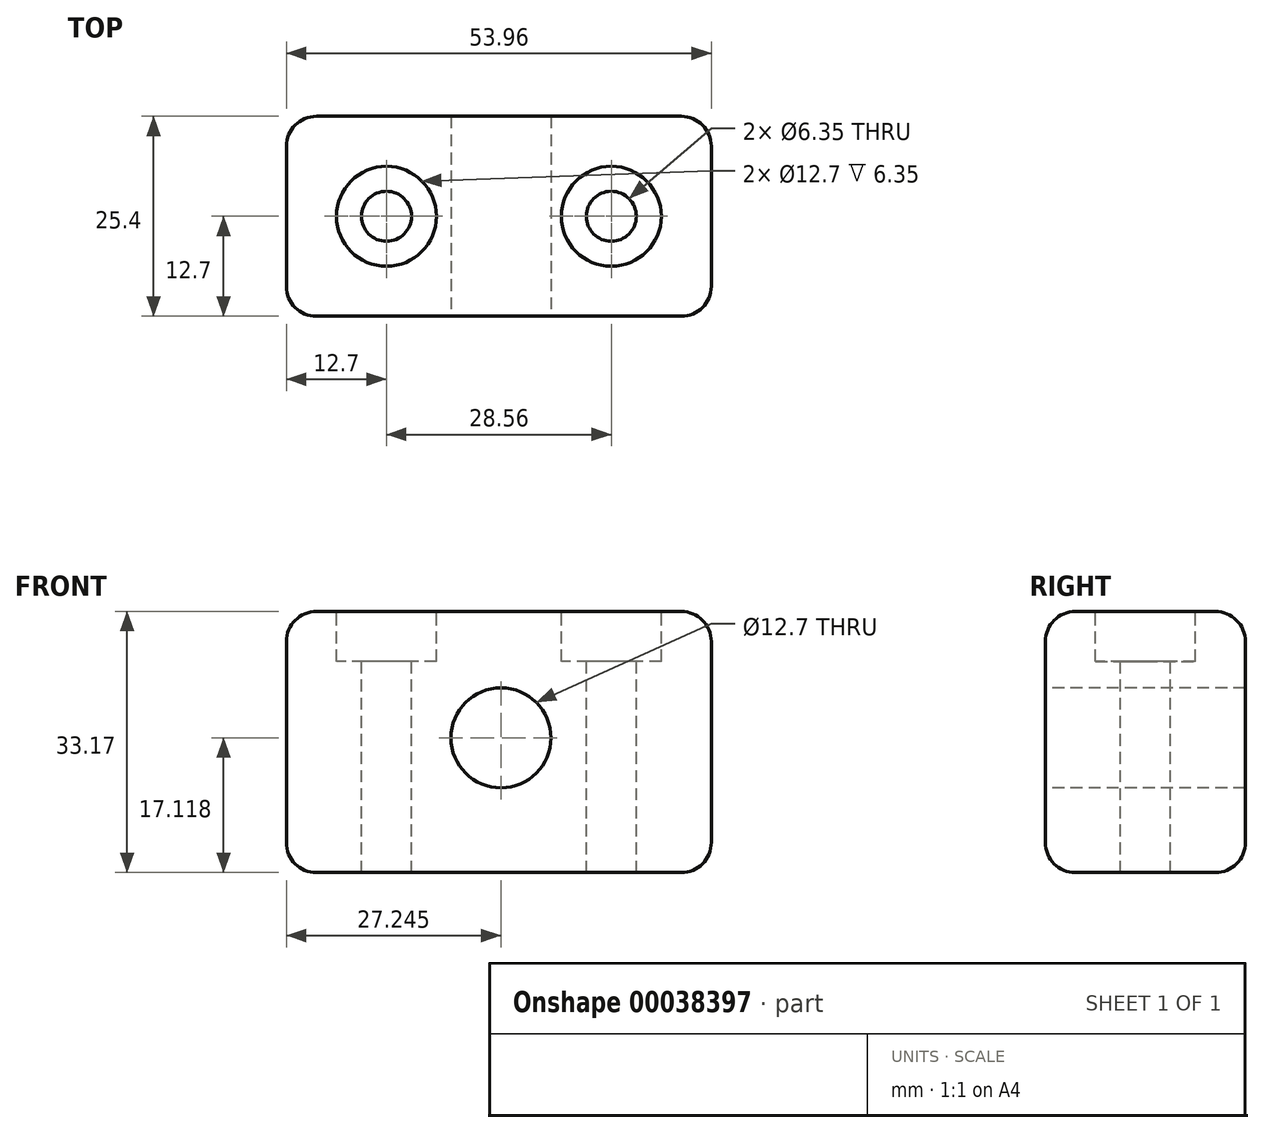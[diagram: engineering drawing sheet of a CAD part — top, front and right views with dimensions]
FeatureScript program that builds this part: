
annotation { "Feature Type Name" : "Feature", "Feature Type Description" : "" }
export const myFeature = defineFeature(function(context is Context, id is Id, definition is map)
    precondition{}
    {
        {
            var Q0;
            Q0=qCreatedBy(makeId("Front.planeOp"),FACE);
            var sketch = newSketch(context, id + "F0", { "sketchPlane" : qUnion([Q0])});
            skLineSegment(sketch, "E0.bottom", {"start": v(0, 0) * mm, "end": v(53.96, 0) * mm});
            skLineSegment(sketch, "E0.top", {"start": v(0, 33.17) * mm, "end": v(53.96, 33.17) * mm});
            skLineSegment(sketch, "E0.left", {"start": v(0, 0) * mm, "end": v(0, 33.17) * mm});
            skLineSegment(sketch, "E0.right", {"start": v(53.96, 0) * mm, "end": v(53.96, 33.17) * mm});
            skSolve(sketch);
        }
        {
            var Q0;
            Q0=makeQuery(id+"F0.imprint","IMPRINT",FACE,{"disambiguationData":[TD([[makeQuery(id+"F0.imprint","IMPRINT",EDGE,{"derivedFrom":sQuery(id+"F0.wireOp",EDGE,"E0.bottom")}),1.0]])]});
            extrude(context, id + "F1", {"entities" : qUnion([Q0]), "depth" : 25.4 * mm});
        }
        {
            var Q0;
            Q0=makeQuery(id+"F1.opExtrude","CAP_EDGE",EDGE,{"disambiguationData":[OSD([sQuery(id+"F0.wireOp",EDGE,"E0.top")])],"isStart":false});
            var Q1;
            Q1=makeQuery(id+"F1.opExtrude","SWEPT_EDGE",EDGE,{"disambiguationData":[OSD([sQuery(id+"F0.wireOp",EDGE,"E0.top"),sQuery(id+"F0.wireOp",EDGE,"E0.right")])]});
            var Q2;
            Q2=makeQuery(id+"F1.opExtrude","CAP_FACE",FACE,{"disambiguationData":[OSD([sQuery(id+"F0.wireOp",EDGE,"E0.bottom"),sQuery(id+"F0.wireOp",EDGE,"E0.top"),sQuery(id+"F0.wireOp",EDGE,"E0.left"),sQuery(id+"F0.wireOp",EDGE,"E0.right")])],"isStart":false});
            var Q3;
            Q3=makeQuery(id+"F1.opExtrude","SWEPT_FACE",FACE,{"disambiguationData":[OSD([sQuery(id+"F0.wireOp",EDGE,"E0.right")])]});
            var Q4;
            Q4=makeQuery(id+"F1.opExtrude","CAP_FACE",FACE,{"disambiguationData":[OSD([sQuery(id+"F0.wireOp",EDGE,"E0.bottom"),sQuery(id+"F0.wireOp",EDGE,"E0.top"),sQuery(id+"F0.wireOp",EDGE,"E0.left"),sQuery(id+"F0.wireOp",EDGE,"E0.right")])],"isStart":true});
            var Q5;
            Q5=makeQuery(id+"F1.opExtrude","SWEPT_FACE",FACE,{"disambiguationData":[OSD([sQuery(id+"F0.wireOp",EDGE,"E0.left")])]});
            fillet(context, id + "F2", {"entities" : qUnion([Q0, Q1, Q2, Q3, Q4, Q5]), "radius" : 3.8 * mm, "tangentPropagation" : true, "allowEdgeOverflow" : false});
        }
        {
            var Q0;
            Q0=makeQuery(id+"F1.opExtrude","CAP_FACE",FACE,{"disambiguationData":[OSD([sQuery(id+"F0.wireOp",EDGE,"E0.bottom"),sQuery(id+"F0.wireOp",EDGE,"E0.top"),sQuery(id+"F0.wireOp",EDGE,"E0.left"),sQuery(id+"F0.wireOp",EDGE,"E0.right")])],"isStart":false});
            var sketch = newSketch(context, id + "F3", { "sketchPlane" : qUnion([Q0])});
            skCircle(sketch, "E1", {"center": v(27.25, 17.12) * mm, "radius": 6.35 * mm});
            skSolve(sketch);
        }
        {
            var Q0;
            Q0=makeQuery(id+"F3.imprint","IMPRINT",FACE,{"disambiguationData":[TD([[makeQuery(id+"F3.imprint","IMPRINT",EDGE,{"derivedFrom":sQuery(id+"F3.wireOp",EDGE,"E1")}),1.0]])]});
            extrude(context, id + "F4", {"entities" : qUnion([Q0]), "operationType" : NewBodyOperationType.REMOVE, "endBound" : BoundingType.THROUGH_ALL, "oppositeDirection" : true, "depth" : 25.4 * mm});
        }
        {
            var Q0;
            Q0=makeQuery(id+"F1.opExtrude","SWEPT_FACE",FACE,{"disambiguationData":[OSD([sQuery(id+"F0.wireOp",EDGE,"E0.top")])]});
            var sketch = newSketch(context, id + "F5", { "sketchPlane" : qUnion([Q0])});
            skPoint(sketch, "E2", {"position": v(12.7, -12.7) * mm});
            skPoint(sketch, "E3", {"position": v(41.26, -12.7) * mm});
            skSolve(sketch);
        }
        {
            var Q0;
            Q0=sQuery(id+"F5.wireOp",VERTEX,"E2");
            var Q1;
            Q1=sQuery(id+"F5.wireOp",VERTEX,"E3");
            var Q2;
            Q2=makeQuery(id+"F1.opExtrude","SWEPT_BODY",BODY,{"disambiguationData":[OSD([sQuery(id+"F0.wireOp",EDGE,"E0.bottom"),sQuery(id+"F0.wireOp",EDGE,"E0.top"),sQuery(id+"F0.wireOp",EDGE,"E0.left"),sQuery(id+"F0.wireOp",EDGE,"E0.right")])]});
            hole(context, id + "F6", {"style" : HoleStyle.C_BORE, "holeDiameter" : 6.35 * mm, "cBoreDiameter" : 12.7 * mm, "cBoreDepth" : 6.35 * mm, "endStyle" : HoleEndStyle.THROUGH, "locations" : qUnion([Q0, Q1]), "scope" : qUnion([Q2])});
        }
    });
